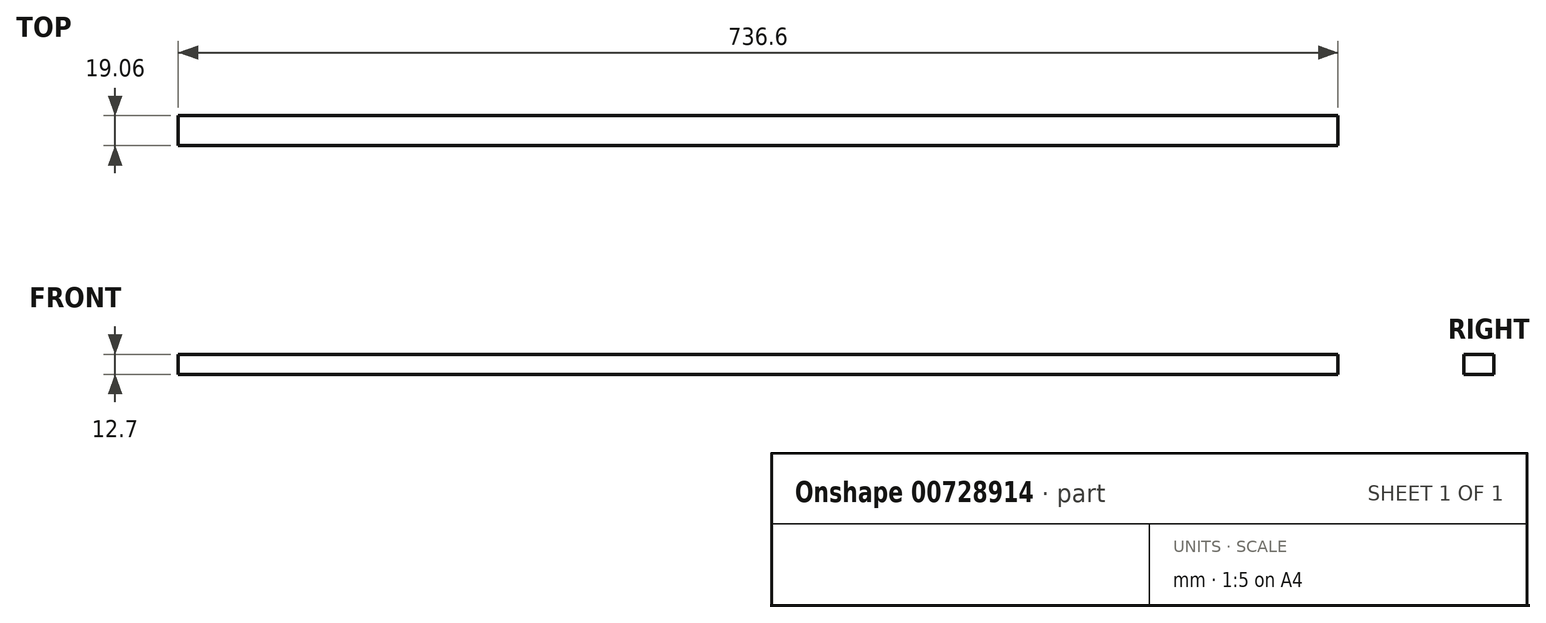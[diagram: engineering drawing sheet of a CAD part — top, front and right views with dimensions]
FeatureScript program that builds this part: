
annotation { "Feature Type Name" : "Feature", "Feature Type Description" : "" }
export const myFeature = defineFeature(function(context is Context, id is Id, definition is map)
    precondition{}
    {
        {
            var Q0;
            Q0=qCreatedBy(makeId("Top.planeOp"),FACE);
            var sketch = newSketch(context, id + "F0", { "sketchPlane" : qUnion([Q0])});
            skLineSegment(sketch, "E0.bottom", {"start": v(368.3, -9.53) * mm, "end": v(-368.3, -9.53) * mm});
            skLineSegment(sketch, "E0.top", {"start": v(368.3, 9.53) * mm, "end": v(-368.3, 9.52) * mm});
            skLineSegment(sketch, "E0.left", {"start": v(368.3, -9.53) * mm, "end": v(368.3, 9.52) * mm});
            skLineSegment(sketch, "E0.right", {"start": v(-368.3, -9.53) * mm, "end": v(-368.3, 9.52) * mm});
            skPoint(sketch, "E0.middle", {"position": v(0, 0) * mm});
            skSolve(sketch);
        }
        {
            var Q0;
            Q0=makeQuery(id+"F0.imprint","IMPRINT",FACE,{"disambiguationData":[TD([[makeQuery(id+"F0.imprint","IMPRINT",EDGE,{"derivedFrom":sQuery(id+"F0.wireOp",EDGE,"E0.bottom")}),-1.0]])]});
            extrude(context, id + "F1", {"entities" : qUnion([Q0]), "oppositeDirection" : true, "depth" : 12.7 * mm, "offsetDistance" : 25.4 * mm});
        }
    });
